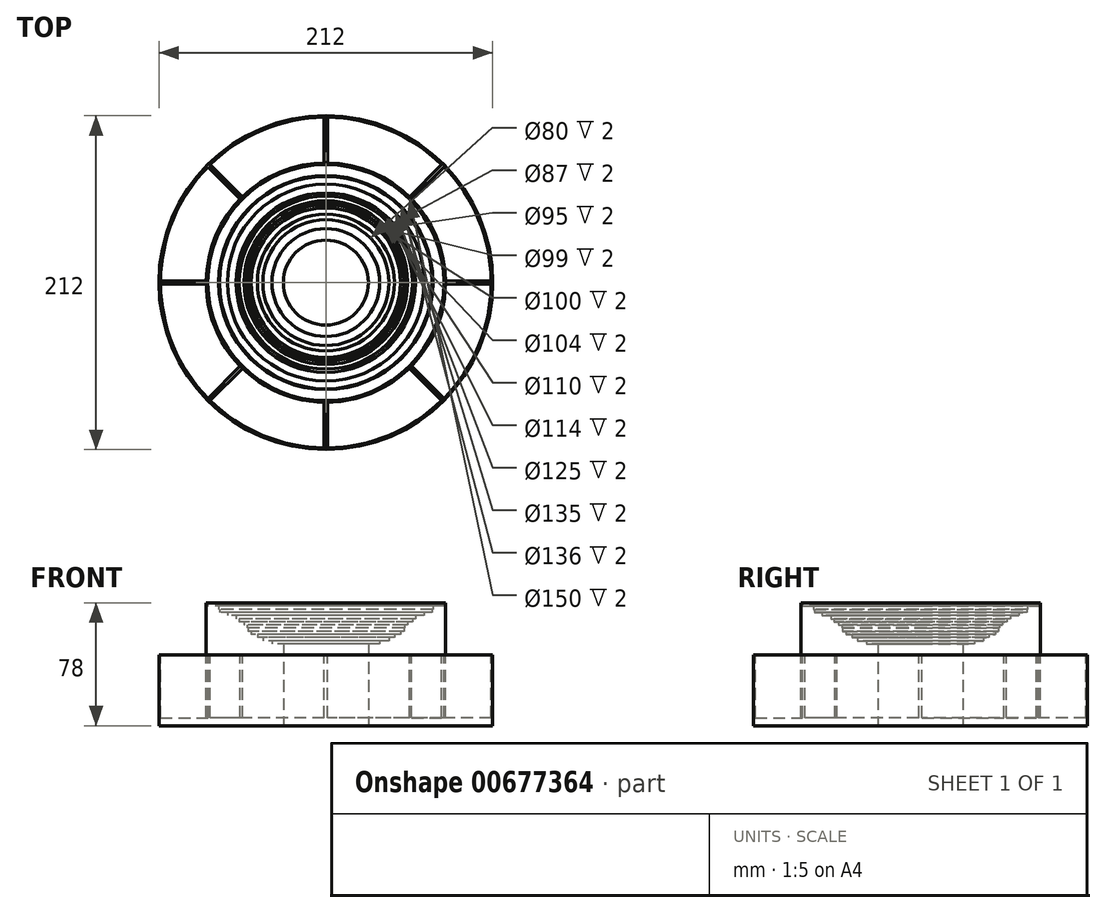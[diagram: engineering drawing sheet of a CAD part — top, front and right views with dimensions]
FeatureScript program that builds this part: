
annotation { "Feature Type Name" : "Feature", "Feature Type Description" : "" }
export const myFeature = defineFeature(function(context is Context, id is Id, definition is map)
    precondition{}
    {
        {
            var Q0;
            Q0=qCreatedBy(makeId("Top.planeOp"),FACE);
            var sketch = newSketch(context, id + "F0", { "sketchPlane" : qUnion([Q0])});
            skCircle(sketch, "E0", {"center": v(0, 0) * mm, "radius": 27 * mm});
            skCircle(sketch, "E1", {"center": v(0, 0) * mm, "radius": 34.25 * mm});
            skSolve(sketch);
        }
        {
            var Q0;
            Q0 = qSketchRegion(id + "F0", true);
            extrude(context, id + "F1", {"entities" : qUnion([Q0]), "depth" : 52 * mm, "offsetDistance" : 25 * mm});
        }
        {
            var Q0;
            Q0=qCreatedBy(makeId("Top.planeOp"),FACE);
            var sketch = newSketch(context, id + "F2", { "sketchPlane" : qUnion([Q0])});
            skCircle(sketch, "E2", {"center": v(0, 0) * mm, "radius": 40 * mm});
            skCircle(sketch, "E3", {"center": v(0, 0) * mm, "radius": 34.25 * mm});
            skSolve(sketch);
        }
        {
            var Q0;
            Q0=makeQuery(id+"F2.imprint","IMPRINT",FACE,{"disambiguationData":[TD([[makeQuery(id+"F2.imprint","IMPRINT",EDGE,{"derivedFrom":sQuery(id+"F2.wireOp",EDGE,"E2")}),1.0]])]});
            extrude(context, id + "F3", {"entities" : qUnion([Q0]), "operationType" : NewBodyOperationType.ADD, "depth" : 54 * mm, "offsetDistance" : 25 * mm});
        }
        {
            var Q0;
            Q0=qCreatedBy(makeId("Top.planeOp"),FACE);
            var sketch = newSketch(context, id + "F4", { "sketchPlane" : qUnion([Q0])});
            skCircle(sketch, "E4", {"center": v(0, 0) * mm, "radius": 43.5 * mm});
            skCircle(sketch, "E5", {"center": v(0, 0) * mm, "radius": 40 * mm});
            skSolve(sketch);
        }
        {
            var Q0;
            Q0 = qSketchRegion(id + "F4", true);
            extrude(context, id + "F5", {"entities" : qUnion([Q0]), "operationType" : NewBodyOperationType.ADD, "depth" : 56 * mm, "offsetDistance" : 25 * mm});
        }
        {
            var Q0;
            Q0=qCreatedBy(makeId("Top.planeOp"),FACE);
            var sketch = newSketch(context, id + "F6", { "sketchPlane" : qUnion([Q0])});
            skCircle(sketch, "E6", {"center": v(0, 0) * mm, "radius": 43.5 * mm});
            skCircle(sketch, "E7", {"center": v(0, 0) * mm, "radius": 47.5 * mm});
            skSolve(sketch);
        }
        {
            var Q0;
            Q0 = qSketchRegion(id + "F6", true);
            extrude(context, id + "F7", {"entities" : qUnion([Q0]), "operationType" : NewBodyOperationType.ADD, "depth" : 58 * mm, "offsetDistance" : 25 * mm});
        }
        {
            var Q0;
            Q0=qCreatedBy(makeId("Top.planeOp"),FACE);
            var sketch = newSketch(context, id + "F8", { "sketchPlane" : qUnion([Q0])});
            skCircle(sketch, "E8", {"center": v(0, 0) * mm, "radius": 47.5 * mm});
            skCircle(sketch, "E9", {"center": v(0, 0) * mm, "radius": 49.5 * mm});
            skSolve(sketch);
        }
        {
            var Q0;
            Q0 = qSketchRegion(id + "F8", true);
            extrude(context, id + "F9", {"entities" : qUnion([Q0]), "operationType" : NewBodyOperationType.ADD, "depth" : 60 * mm, "offsetDistance" : 25 * mm});
        }
        {
            var Q0;
            Q0=qCreatedBy(makeId("Top.planeOp"),FACE);
            var sketch = newSketch(context, id + "F10", { "sketchPlane" : qUnion([Q0])});
            skCircle(sketch, "E10", {"center": v(0, 0) * mm, "radius": 49.5 * mm});
            skCircle(sketch, "E11", {"center": v(0, 0) * mm, "radius": 50 * mm});
            skSolve(sketch);
        }
        {
            var Q0;
            Q0 = qSketchRegion(id + "F10", true);
            extrude(context, id + "F11", {"entities" : qUnion([Q0]), "operationType" : NewBodyOperationType.ADD, "depth" : 62 * mm, "offsetDistance" : 25 * mm});
        }
        {
            var Q0;
            Q0=qCreatedBy(makeId("Top.planeOp"),FACE);
            var sketch = newSketch(context, id + "F12", { "sketchPlane" : qUnion([Q0])});
            skCircle(sketch, "E12", {"center": v(0, 0) * mm, "radius": 50 * mm});
            skCircle(sketch, "E13", {"center": v(0, 0) * mm, "radius": 52 * mm});
            skSolve(sketch);
        }
        {
            var Q0;
            Q0 = qSketchRegion(id + "F12", true);
            extrude(context, id + "F13", {"entities" : qUnion([Q0]), "operationType" : NewBodyOperationType.ADD, "depth" : 64 * mm, "offsetDistance" : 25 * mm});
        }
        {
            var Q0;
            Q0=qCreatedBy(makeId("Top.planeOp"),FACE);
            var sketch = newSketch(context, id + "F14", { "sketchPlane" : qUnion([Q0])});
            skCircle(sketch, "E14", {"center": v(0, 0) * mm, "radius": 52 * mm});
            skCircle(sketch, "E15", {"center": v(0, 0) * mm, "radius": 55 * mm});
            skSolve(sketch);
        }
        {
            var Q0;
            Q0 = qSketchRegion(id + "F14", true);
            extrude(context, id + "F15", {"entities" : qUnion([Q0]), "operationType" : NewBodyOperationType.ADD, "depth" : 66 * mm, "offsetDistance" : 25 * mm});
        }
        {
            var Q0;
            Q0=qCreatedBy(makeId("Top.planeOp"),FACE);
            var sketch = newSketch(context, id + "F16", { "sketchPlane" : qUnion([Q0])});
            skCircle(sketch, "E16", {"center": v(0, 0) * mm, "radius": 55 * mm});
            skCircle(sketch, "E17", {"center": v(0, 0) * mm, "radius": 57 * mm});
            skSolve(sketch);
        }
        {
            var Q0;
            Q0 = qSketchRegion(id + "F16", true);
            extrude(context, id + "F17", {"entities" : qUnion([Q0]), "operationType" : NewBodyOperationType.ADD, "depth" : 68 * mm, "offsetDistance" : 25 * mm});
        }
        {
            var Q0;
            Q0=qCreatedBy(makeId("Top.planeOp"),FACE);
            var sketch = newSketch(context, id + "F18", { "sketchPlane" : qUnion([Q0])});
            skCircle(sketch, "E18", {"center": v(0, 0) * mm, "radius": 57 * mm});
            skCircle(sketch, "E19", {"center": v(0, 0) * mm, "radius": 62.5 * mm});
            skSolve(sketch);
        }
        {
            var Q0;
            Q0 = qSketchRegion(id + "F18", true);
            extrude(context, id + "F19", {"entities" : qUnion([Q0]), "operationType" : NewBodyOperationType.ADD, "depth" : 70 * mm, "offsetDistance" : 25 * mm});
        }
        {
            var Q0;
            Q0=qCreatedBy(makeId("Top.planeOp"),FACE);
            var sketch = newSketch(context, id + "F20", { "sketchPlane" : qUnion([Q0])});
            skCircle(sketch, "E20", {"center": v(0, 0) * mm, "radius": 62.5 * mm});
            skCircle(sketch, "E21", {"center": v(0, 0) * mm, "radius": 67.5 * mm});
            skSolve(sketch);
        }
        {
            var Q0;
            Q0 = qSketchRegion(id + "F20", true);
            extrude(context, id + "F21", {"entities" : qUnion([Q0]), "operationType" : NewBodyOperationType.ADD, "depth" : 72 * mm, "offsetDistance" : 25 * mm});
        }
        {
            var Q0;
            Q0=qCreatedBy(makeId("Top.planeOp"),FACE);
            var sketch = newSketch(context, id + "F22", { "sketchPlane" : qUnion([Q0])});
            skCircle(sketch, "E22", {"center": v(0, 0) * mm, "radius": 67.5 * mm});
            skCircle(sketch, "E23", {"center": v(0, 0) * mm, "radius": 68 * mm});
            skSolve(sketch);
        }
        {
            var Q0;
            Q0 = qSketchRegion(id + "F22", true);
            extrude(context, id + "F23", {"entities" : qUnion([Q0]), "operationType" : NewBodyOperationType.ADD, "depth" : 74 * mm, "offsetDistance" : 25 * mm});
        }
        {
            var Q0;
            Q0=qCreatedBy(makeId("Top.planeOp"),FACE);
            var sketch = newSketch(context, id + "F24", { "sketchPlane" : qUnion([Q0])});
            skCircle(sketch, "E24", {"center": v(0, 0) * mm, "radius": 68 * mm});
            skCircle(sketch, "E25", {"center": v(0, 0) * mm, "radius": 75 * mm});
            skSolve(sketch);
        }
        {
            var Q0;
            Q0 = qSketchRegion(id + "F24", true);
            extrude(context, id + "F25", {"entities" : qUnion([Q0]), "operationType" : NewBodyOperationType.ADD, "depth" : 76 * mm, "offsetDistance" : 25 * mm});
        }
        {
            var Q0;
            Q0=qCreatedBy(makeId("Top.planeOp"),FACE);
            var sketch = newSketch(context, id + "F26", { "sketchPlane" : qUnion([Q0])});
            skCircle(sketch, "E26", {"center": v(0, 0) * mm, "radius": 75 * mm});
            skCircle(sketch, "E27", {"center": v(0, 0) * mm, "radius": 76 * mm});
            skSolve(sketch);
        }
        {
            var Q0;
            Q0 = qSketchRegion(id + "F26", true);
            extrude(context, id + "F27", {"entities" : qUnion([Q0]), "operationType" : NewBodyOperationType.ADD, "depth" : 78 * mm, "offsetDistance" : 25 * mm});
        }
        {
            var Q0;
            Q0=qCreatedBy(makeId("Top.planeOp"),FACE);
            var sketch = newSketch(context, id + "F28", { "sketchPlane" : qUnion([Q0])});
            skCircle(sketch, "E28", {"center": v(0, 0) * mm, "radius": 76 * mm});
            skCircle(sketch, "E29", {"center": v(0, 0) * mm, "radius": 105 * mm});
            skLineSegment(sketch, "E30", {"start": v(0, 76) * mm, "end": v(0, 105) * mm});
            skLineSegment(sketch, "E31", {"start": v(76, 0) * mm, "end": v(105, 0) * mm});
            skLineSegment(sketch, "E32", {"start": v(0, -76) * mm, "end": v(0, -105) * mm});
            skLineSegment(sketch, "E33", {"start": v(-76, 0) * mm, "end": v(-105, 0) * mm});
            skLineSegment(sketch, "E34", {"start": v(-51.9, 55.53) * mm, "end": v(-72.4, 76.04) * mm});
            skLineSegment(sketch, "E35.1.0", {"start": v(-55.53, -51.9) * mm, "end": v(-76.04, -72.4) * mm});
            skLineSegment(sketch, "E35.2.0", {"start": v(51.9, -55.53) * mm, "end": v(72.4, -76.04) * mm});
            skLineSegment(sketch, "E35.3.0", {"start": v(55.53, 51.9) * mm, "end": v(76.04, 72.4) * mm});
            skSolve(sketch);
        }
        {
            var Q0;
            Q0 = qSketchRegion(id + "F28", true);
            extrude(context, id + "F29", {"entities" : qUnion([Q0]), "operationType" : NewBodyOperationType.ADD, "depth" : 45 * mm, "offsetDistance" : 25 * mm});
        }
        {
            var Q0;
            Q0=makeQuery(id+"F29.opExtrude","CAP_FACE",FACE,{"disambiguationData":[OSD([sQuery(id+"F28.wireOp",EDGE,"E28"),sQuery(id+"F28.wireOp",EDGE,"E29")])],"isStart":false});
            var sketch = newSketch(context, id + "F30", { "sketchPlane" : qUnion([Q0])});
            skCircle(sketch, "E36", {"center": v(0, 0) * mm, "radius": 76 * mm});
            skCircle(sketch, "E37", {"center": v(0, 0) * mm, "radius": 105 * mm});
            skLineSegment(sketch, "E38", {"start": v(0, 108.8) * mm, "end": v(1, 108.8) * mm, "construction": true});
            skLineSegment(sketch, "E39", {"start": v(0, 108.8) * mm, "end": v(-1, 108.8) * mm, "construction": true});
            skLineSegment(sketch, "E40", {"start": v(0, 73.2) * mm, "end": v(1, 73.2) * mm, "construction": true});
            skLineSegment(sketch, "E41", {"start": v(0, 73.2) * mm, "end": v(-1, 73.2) * mm, "construction": true});
            skLineSegment(sketch, "E42", {"start": v(-1, 105) * mm, "end": v(-1, 76) * mm});
            skLineSegment(sketch, "E43", {"start": v(1, 76) * mm, "end": v(1, 105) * mm});
            skLineSegment(sketch, "E44.1.0", {"start": v(-74.95, 73.54) * mm, "end": v(-54.44, 53.03) * mm});
            skLineSegment(sketch, "E44.1.1", {"start": v(-53.03, 54.44) * mm, "end": v(-73.54, 74.95) * mm});
            skLineSegment(sketch, "E44.2.0", {"start": v(-105, -1) * mm, "end": v(-76, -1) * mm});
            skLineSegment(sketch, "E44.2.1", {"start": v(-76, 1) * mm, "end": v(-105, 1) * mm});
            skLineSegment(sketch, "E44.3.0", {"start": v(-73.54, -74.95) * mm, "end": v(-53.03, -54.44) * mm});
            skLineSegment(sketch, "E44.3.1", {"start": v(-54.44, -53.03) * mm, "end": v(-74.95, -73.54) * mm});
            skLineSegment(sketch, "E44.4.0", {"start": v(1, -105) * mm, "end": v(1, -76) * mm});
            skLineSegment(sketch, "E44.4.1", {"start": v(-1, -76) * mm, "end": v(-1, -105) * mm});
            skLineSegment(sketch, "E44.5.0", {"start": v(74.95, -73.54) * mm, "end": v(54.44, -53.03) * mm});
            skLineSegment(sketch, "E44.5.1", {"start": v(53.03, -54.44) * mm, "end": v(73.54, -74.95) * mm});
            skLineSegment(sketch, "E44.6.0", {"start": v(105, 1) * mm, "end": v(76, 1) * mm});
            skLineSegment(sketch, "E44.6.1", {"start": v(76, -1) * mm, "end": v(105, -1) * mm});
            skLineSegment(sketch, "E44.7.0", {"start": v(73.54, 74.95) * mm, "end": v(53.03, 54.44) * mm});
            skLineSegment(sketch, "E44.7.1", {"start": v(54.44, 53.03) * mm, "end": v(74.95, 73.54) * mm});
            skCircle(sketch, "E45", {"center": v(0, 0) * mm, "radius": 106 * mm});
            skSolve(sketch);
        }
        {
            var Q0;
            Q0=makeQuery(id+"F30.imprint","IMPRINT",FACE,{"disambiguationData":[TD([[makeQuery(id+"F30.imprint","IMPRINT",EDGE,{"derivedFrom":sQuery(id+"F30.wireOp",EDGE,"E45")}),1.0]])]});
            extrude(context, id + "F31", {"entities" : qUnion([Q0]), "operationType" : NewBodyOperationType.ADD, "oppositeDirection" : true, "depth" : 45 * mm, "offsetDistance" : 25 * mm});
        }
        {
            var Q0;
            {var subQ0=sQuery(id+"F30.wireOp",EDGE,"E44.2.0");Q0=makeQuery(id+"F30.imprint","IMPRINT",FACE,{"disambiguationData":[TD([[makeQuery(id+"F30.imprint","IMPRINT",EDGE,{"derivedFrom":subQ0}),-1.0]])]});}
            var Q1;
            {var subQ0=sQuery(id+"F30.wireOp",EDGE,"E44.1.0");Q1=makeQuery(id+"F30.imprint","IMPRINT",FACE,{"disambiguationData":[TD([[makeQuery(id+"F30.imprint","IMPRINT",EDGE,{"derivedFrom":subQ0}),-1.0]])]});}
            var Q2;
            {var subQ0=sQuery(id+"F30.wireOp",EDGE,"E42");Q2=makeQuery(id+"F30.imprint","IMPRINT",FACE,{"disambiguationData":[TD([[makeQuery(id+"F30.imprint","IMPRINT",EDGE,{"derivedFrom":subQ0}),-1.0]])]});}
            var Q3;
            {var subQ0=sQuery(id+"F30.wireOp",EDGE,"E43");Q3=makeQuery(id+"F30.imprint","IMPRINT",FACE,{"disambiguationData":[TD([[makeQuery(id+"F30.imprint","IMPRINT",EDGE,{"derivedFrom":subQ0}),-1.0]])]});}
            var Q4;
            {var subQ0=sQuery(id+"F30.wireOp",EDGE,"E44.6.0");Q4=makeQuery(id+"F30.imprint","IMPRINT",FACE,{"disambiguationData":[TD([[makeQuery(id+"F30.imprint","IMPRINT",EDGE,{"derivedFrom":subQ0}),-1.0]])]});}
            var Q5;
            {var subQ0=sQuery(id+"F30.wireOp",EDGE,"E44.5.0");Q5=makeQuery(id+"F30.imprint","IMPRINT",FACE,{"disambiguationData":[TD([[makeQuery(id+"F30.imprint","IMPRINT",EDGE,{"derivedFrom":subQ0}),-1.0]])]});}
            var Q6;
            {var subQ0=sQuery(id+"F30.wireOp",EDGE,"E44.4.0");Q6=makeQuery(id+"F30.imprint","IMPRINT",FACE,{"disambiguationData":[TD([[makeQuery(id+"F30.imprint","IMPRINT",EDGE,{"derivedFrom":subQ0}),-1.0]])]});}
            var Q7;
            {var subQ0=sQuery(id+"F30.wireOp",EDGE,"E44.3.0");Q7=makeQuery(id+"F30.imprint","IMPRINT",FACE,{"disambiguationData":[TD([[makeQuery(id+"F30.imprint","IMPRINT",EDGE,{"derivedFrom":subQ0}),-1.0]])]});}
            extrude(context, id + "F32", {"entities" : qUnion([Q0, Q1, Q2, Q3, Q4, Q5, Q6, Q7]), "operationType" : NewBodyOperationType.REMOVE, "oppositeDirection" : true, "depth" : 40 * mm, "offsetDistance" : 25 * mm});
        }
    });
